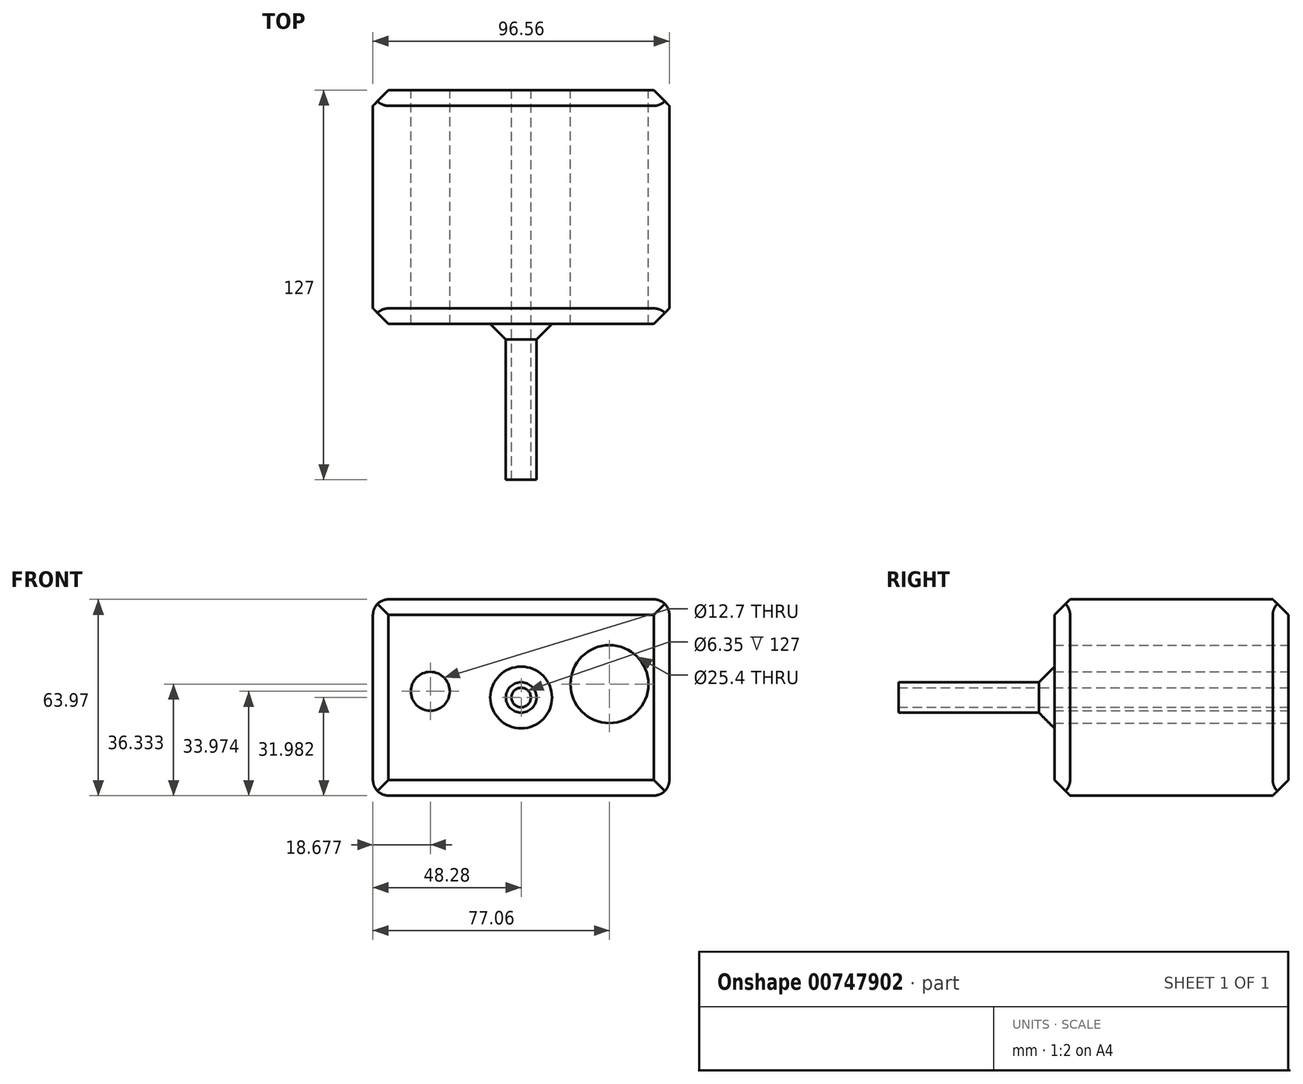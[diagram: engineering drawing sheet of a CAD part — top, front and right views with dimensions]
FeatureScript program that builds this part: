
annotation { "Feature Type Name" : "Feature", "Feature Type Description" : "" }
export const myFeature = defineFeature(function(context is Context, id is Id, definition is map)
    precondition{}
    {
        {
            var Q0;
            Q0=qCreatedBy(makeId("Front.planeOp"),FACE);
            var sketch = newSketch(context, id + "F0", { "sketchPlane" : qUnion([Q0])});
            skLineSegment(sketch, "E0.bottom", {"start": v(48.28, 63.67) * mm, "end": v(-48.28, 63.67) * mm});
            skLineSegment(sketch, "E0.top", {"start": v(48.28, -0.3) * mm, "end": v(-48.28, -0.3) * mm});
            skLineSegment(sketch, "E0.left", {"start": v(48.28, 63.67) * mm, "end": v(48.28, -0.3) * mm});
            skLineSegment(sketch, "E0.right", {"start": v(-48.28, 63.67) * mm, "end": v(-48.28, -0.3) * mm});
            skPoint(sketch, "E0.middle", {"position": v(0, 31.68) * mm});
            skPoint(sketch, "E1", {"position": v(-29.6, 33.67) * mm});
            skPoint(sketch, "E2", {"position": v(28.78, 36.03) * mm});
            skSolve(sketch);
        }
        {
            var Q0;
            Q0=makeQuery(id+"F0.imprint","IMPRINT",FACE,{"disambiguationData":[TD([[makeQuery(id+"F0.imprint","IMPRINT",EDGE,{"derivedFrom":sQuery(id+"F0.wireOp",EDGE,"E0.bottom")}),1.0]])]});
            extrude(context, id + "F1", {"entities" : qUnion([Q0]), "depth" : 76.2 * mm, "offsetDistance" : 25.4 * mm});
        }
        {
            var Q0;
            Q0=makeQuery(id+"F1.opExtrude","CAP_FACE",FACE,{"disambiguationData":[OSD([sQuery(id+"F0.wireOp",EDGE,"E0.bottom"),sQuery(id+"F0.wireOp",EDGE,"E0.top"),sQuery(id+"F0.wireOp",EDGE,"E0.left"),sQuery(id+"F0.wireOp",EDGE,"E0.right")])],"isStart":false});
            var sketch = newSketch(context, id + "F2", { "sketchPlane" : qUnion([Q0])});
            skCircle(sketch, "E3", {"center": v(0, 31.68) * mm, "radius": 4.97 * mm});
            skPoint(sketch, "E3.centerSnap0", {"position": v(48.28, 31.68) * mm});
            skSolve(sketch);
        }
        {
            var Q0;
            Q0 = qSketchRegion(id + "F2", true);
            extrude(context, id + "F3", {"entities" : qUnion([Q0]), "operationType" : NewBodyOperationType.ADD, "depth" : 50.8 * mm, "offsetDistance" : 25.4 * mm});
        }
        {
            var Q0;
            Q0=makeQuery(id+"F1.opExtrude","CAP_FACE",FACE,{"disambiguationData":[OSD([sQuery(id+"F0.wireOp",EDGE,"E0.bottom"),sQuery(id+"F0.wireOp",EDGE,"E0.top"),sQuery(id+"F0.wireOp",EDGE,"E0.left"),sQuery(id+"F0.wireOp",EDGE,"E0.right")])],"isStart":false});
            chamfer(context, id + "F4", {"entities" : qUnion([Q0]), "width" : 5.08 * mm, "tangentPropagation" : true});
        }
        {
            var Q0;
            Q0=makeQuery(id+"F1.opExtrude","CAP_FACE",FACE,{"disambiguationData":[OSD([sQuery(id+"F0.wireOp",EDGE,"E0.bottom"),sQuery(id+"F0.wireOp",EDGE,"E0.top"),sQuery(id+"F0.wireOp",EDGE,"E0.left"),sQuery(id+"F0.wireOp",EDGE,"E0.right")])],"isStart":true});
            chamfer(context, id + "F5", {"entities" : qUnion([Q0]), "width" : 5.08 * mm, "tangentPropagation" : true});
        }
        {
            var Q0;
            Q0=sQuery(id+"F0.wireOp",VERTEX,"E1");
            var Q1;
            Q1=makeQuery(id+"F1.opExtrude","SWEPT_BODY",BODY,{"disambiguationData":[OSD([sQuery(id+"F0.wireOp",EDGE,"E0.bottom"),sQuery(id+"F0.wireOp",EDGE,"E0.top"),sQuery(id+"F0.wireOp",EDGE,"E0.left"),sQuery(id+"F0.wireOp",EDGE,"E0.right")])]});
            hole(context, id + "F6", {"style" : HoleStyle.SIMPLE, "endStyle" : HoleEndStyle.THROUGH, "oppositeDirection" : true, "holeDiameter" : 12.7 * mm, "majorDiameter" : 6.35 * mm, "isTappedThrough" : true, "tappedDepth" : 12.7 * mm, "tapClearance" : 3, "locations" : qUnion([Q0]), "scope" : qUnion([Q1])});
        }
        {
            var Q0;
            Q0=sQuery(id+"F0.wireOp",VERTEX,"E0.middle");
            var Q1;
            Q1=makeQuery(id+"F1.opExtrude","SWEPT_BODY",BODY,{"disambiguationData":[OSD([sQuery(id+"F0.wireOp",EDGE,"E0.bottom"),sQuery(id+"F0.wireOp",EDGE,"E0.top"),sQuery(id+"F0.wireOp",EDGE,"E0.left"),sQuery(id+"F0.wireOp",EDGE,"E0.right")])]});
            hole(context, id + "F7", {"style" : HoleStyle.SIMPLE, "endStyle" : HoleEndStyle.THROUGH, "oppositeDirection" : true, "holeDiameter" : 6.35 * mm, "majorDiameter" : 6.35 * mm, "isTappedThrough" : true, "tappedDepth" : 12.7 * mm, "tapClearance" : 3, "locations" : qUnion([Q0]), "scope" : qUnion([Q1])});
        }
        {
            var Q0;
            Q0=makeQuery(id+"F1.opExtrude","SWEPT_EDGE",EDGE,{"disambiguationData":[OSD([sQuery(id+"F0.wireOp",EDGE,"E0.top"),sQuery(id+"F0.wireOp",EDGE,"E0.right")])]});
            fillet(context, id + "F8", {"entities" : qUnion([Q0]), "radius" : 5.08 * mm, "tangentPropagation" : true, "allowEdgeOverflow" : false});
        }
        {
            var Q0;
            Q0=makeQuery(id+"F1.opExtrude","SWEPT_EDGE",EDGE,{"disambiguationData":[OSD([sQuery(id+"F0.wireOp",EDGE,"E0.top"),sQuery(id+"F0.wireOp",EDGE,"E0.left")])]});
            var Q1;
            Q1=makeQuery(id+"F1.opExtrude","SWEPT_EDGE",EDGE,{"disambiguationData":[OSD([sQuery(id+"F0.wireOp",EDGE,"E0.bottom"),sQuery(id+"F0.wireOp",EDGE,"E0.left")])]});
            var Q2;
            Q2=makeQuery(id+"F1.opExtrude","SWEPT_EDGE",EDGE,{"disambiguationData":[OSD([sQuery(id+"F0.wireOp",EDGE,"E0.bottom"),sQuery(id+"F0.wireOp",EDGE,"E0.right")])]});
            fillet(context, id + "F9", {"entities" : qUnion([Q0, Q1, Q2]), "radius" : 5.08 * mm, "tangentPropagation" : true, "allowEdgeOverflow" : false});
        }
        {
            var Q0;
            Q0=sQuery(id+"F0.wireOp",VERTEX,"E2");
            var Q1;
            Q1=makeQuery(id+"F1.opExtrude","SWEPT_BODY",BODY,{"disambiguationData":[OSD([sQuery(id+"F0.wireOp",EDGE,"E0.bottom"),sQuery(id+"F0.wireOp",EDGE,"E0.top"),sQuery(id+"F0.wireOp",EDGE,"E0.left"),sQuery(id+"F0.wireOp",EDGE,"E0.right")])]});
            hole(context, id + "F10", {"style" : HoleStyle.SIMPLE, "endStyle" : HoleEndStyle.THROUGH, "oppositeDirection" : true, "holeDiameter" : 25.4 * mm, "majorDiameter" : 6.35 * mm, "isTappedThrough" : true, "tappedDepth" : 12.7 * mm, "tapClearance" : 3, "locations" : qUnion([Q0]), "scope" : qUnion([Q1])});
        }
    });
